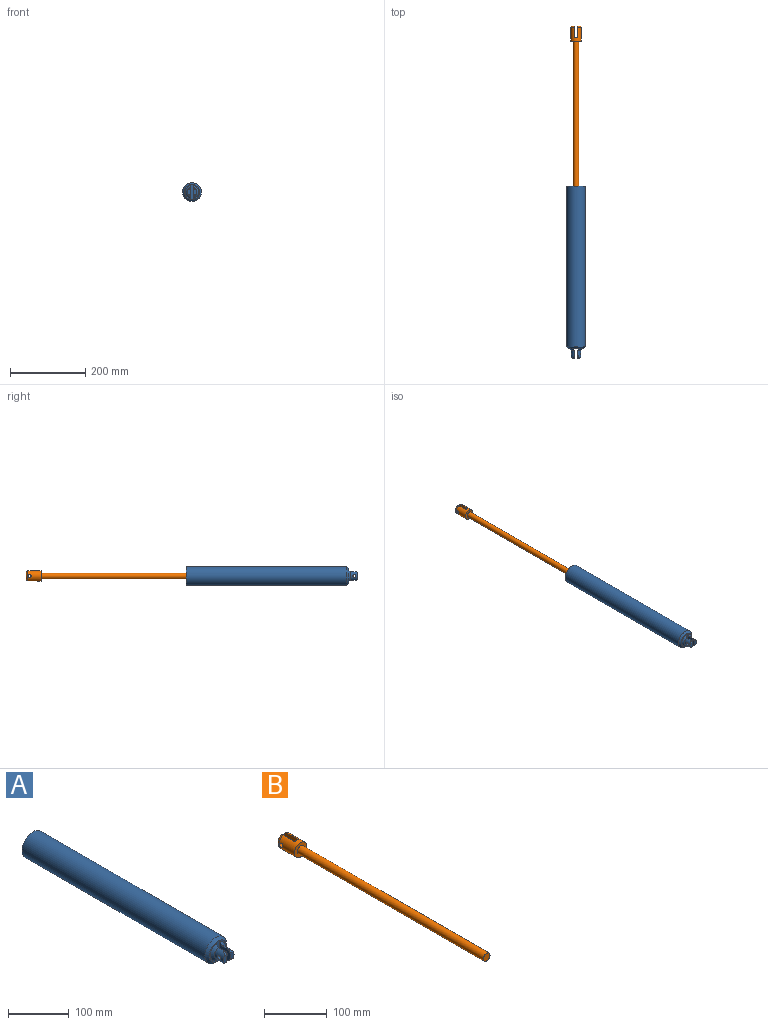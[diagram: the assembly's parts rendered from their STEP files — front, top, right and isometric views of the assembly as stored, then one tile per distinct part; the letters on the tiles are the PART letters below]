
ASSEMBLY  parts=2 mates=1
PART A: 20 faces, bbox 50.2x455.2x50.2 mm
  f0: cylinder r=12.5mm len=23.69mm, axis (0,1,0), area 517.7mm2, adj f1,f2,f12,f14,f18,f19
  f1: plane 34.32x25.24mm, normal (-1,0,0), area 540.9mm2, adj f0,f2,f6,f12,f14,f18,f19
  f2: plane 13.64x8.5mm, normal (0,-1,0), area 107mm2, adj f0,f1,f18,f19
  f3: plane 34.32x25.24mm, normal (1,0,0), area 540.9mm2, adj f4,f5,f6,f11,f13,f16,f17
  f4: cylinder r=12.5mm len=23.69mm, axis (0,1,0), area 517.6mm2, adj f3,f5,f11,f13,f16,f17
  f5: plane 13.64x8.5mm, normal (0,-1,0), area 107mm2, adj f3,f4,f16,f17
  f6: plane 40x40mm, normal (0,-1,0), area 572.1mm2, adj f1,f3,f13,f14,f15
  f7: cylinder r=7.5mm len=420mm, axis (0,1,0), area 19792mm2, adj f9,f10
  f8: cylinder r=25mm len=425mm, axis (0,1,0), area 66758.8mm2, adj f9,f15
  f9: plane 50x50mm, normal (0,1,0), area 1786.8mm2, adj f7,f8
  f10: plane 15x15mm, normal (0,1,0), area 176.7mm2, adj f7
  f11: cylinder r=4mm len=8.5mm, axis (1,0,0), area 205.4mm2, adj f3,f4
  f12: cylinder r=4mm len=8.5mm, axis (1,0,0), area 205.4mm2, adj f0,f1
  f13: cone r=12.5mm half-angle=45deg, axis (0,1,0), area 274.8mm2, adj f3,f4,f6
  f14: cone r=12.5mm half-angle=45deg, axis (0,1,0), area 274.8mm2, adj f0,f1,f6
  f15: cone r=20mm half-angle=45deg, axis (0,1,0), area 999.6mm2, adj f6,f8
  f16: cylinder r=12.1mm len=7.5mm, axis (1,0,0), area 30mm2, adj f3,f4,f5
  f17: cylinder r=12.1mm len=7.5mm, axis (1,0,0), area 30mm2, adj f3,f4,f5
  f18: cylinder r=12.1mm len=7.5mm, axis (1,0,0), area 30mm2, adj f0,f1,f2
  f19: cylinder r=12.1mm len=7.5mm, axis (1,0,0), area 30mm2, adj f0,f1,f2
PART B: 13 faces, bbox 30x460x28.7 mm
  f0: plane 15.82x4.86mm, normal (0,1,0), area 55mm2, adj f2,f9
  f1: cylinder r=13.86mm len=35mm, axis (0,1,0), area 2525.8mm2, adj f2,f6,f7,f8,f9,f10,f11,f12
  f2: torus R=8.86mm, axis (0,-1,0), area 233.1mm2, adj f0,f1,f9
  f3: cylinder r=7.5mm len=420mm, axis (0,-1,0), area 19792mm2, adj f4,f6
  f4: plane 15x15mm, normal (0,-1,0), area 176.7mm2, adj f3
  f5: plane 15.82x4.86mm, normal (0,1,0), area 55mm2, adj f7,f10
  f6: plane 27.72x27.72mm, normal (0,-1,0), area 427mm2, adj f1,f3
  f7: torus R=8.86mm, axis (0,-1,0), area 233.1mm2, adj f1,f5,f10
  f8: cylinder r=25mm len=27.73mm, axis (1,0,0), area 231.4mm2, adj f1,f9,f10
  f9: plane 35x26.55mm, normal (1,0,0), area 834.9mm2, adj f0,f1,f2,f8,f12
  f10: plane 35x26.55mm, normal (-1,0,0), area 834.9mm2, adj f1,f5,f7,f8,f11
  f11: cylinder r=4mm len=9.86mm, axis (1,0,0), area 240.5mm2, adj f1,f10
  f12: cylinder r=4mm len=9.86mm, axis (1,0,0), area 240.5mm2, adj f1,f9
PLACE A at identity fixed
PLACE B t=(0,175,0)mm
MATE slider A.f8 <-> B.f3  axis (0,1,0) through (0,210,0)mm
